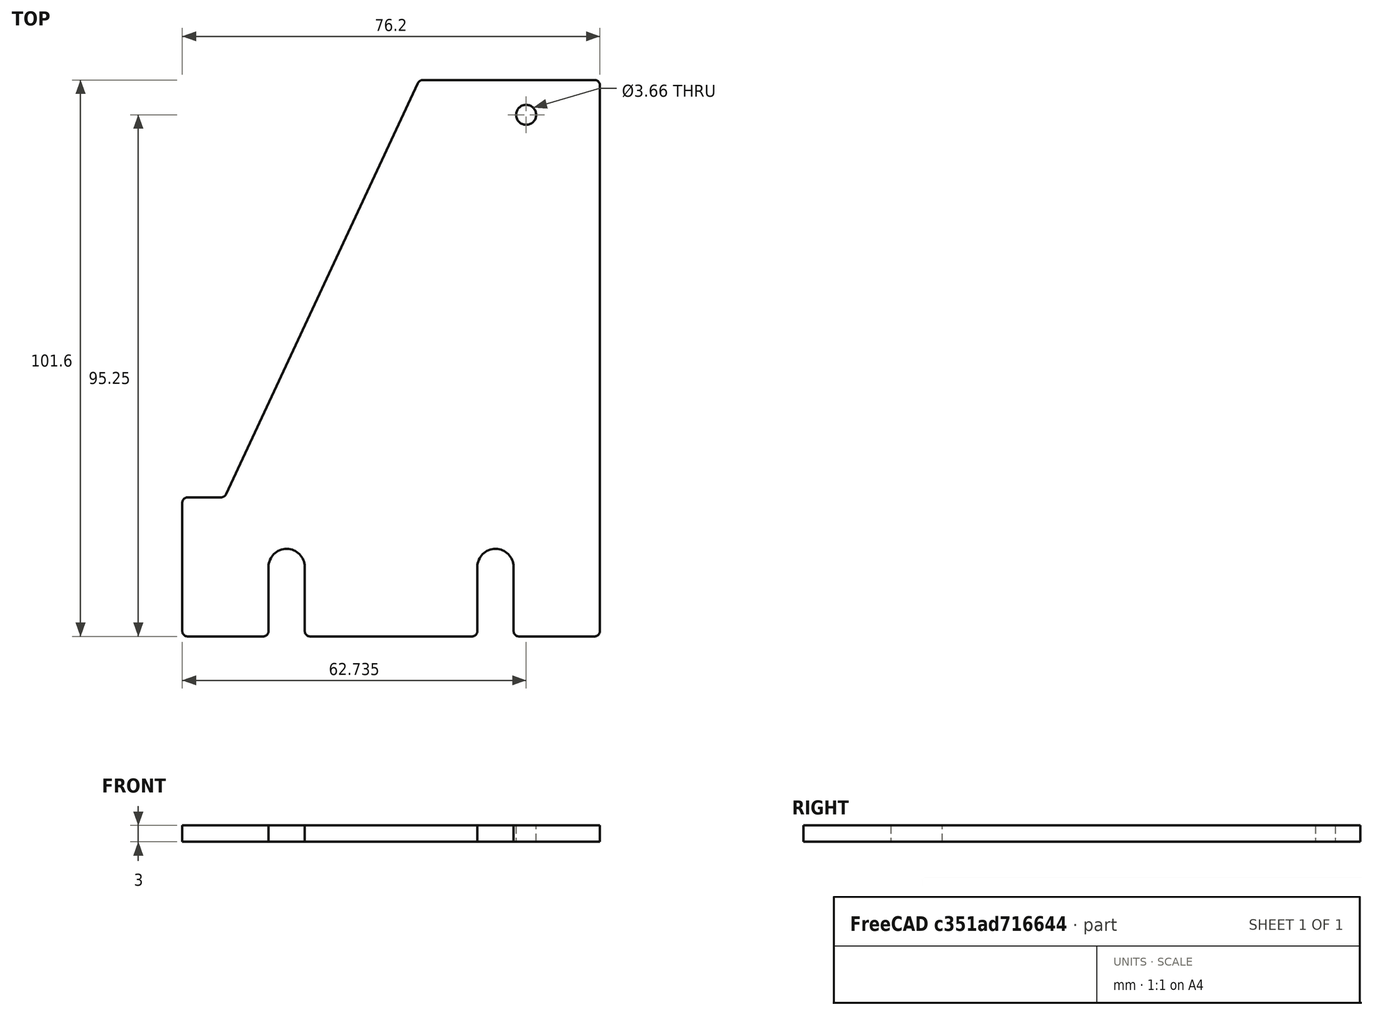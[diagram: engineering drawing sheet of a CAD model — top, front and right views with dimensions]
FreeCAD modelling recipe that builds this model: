
FCSTD DOCUMENT  (FreeCAD 0.21R33675 (Git))
Label: plain_wall_3in_with_door_angled_door_gap
License: All rights reserved
LicenseURL: http://en.wikipedia.org/wiki/All_rights_reserved
objects: Sketcher::SketchObject×1, Spreadsheet::Sheet×1, PartDesign::Pad×1, PartDesign::Body×1
note: 4 computed .brp shape members not serialized (recipe doc carries the construction recipe); baked Part::Feature solids carry a one-line shape summary decoded from their .brp

FEATURE [Sketcher::SketchObject] Sketch
  FullyConstrained = true
  MapMode = 5
  Support = -> [XY_Plane]
  expr: Constraints[15] = Spreadsheet.FilletRadius
  expr: Constraints[17] = Spreadsheet.Height
  expr: Constraints[22] = Spreadsheet.MountHoleDistanceFromBottom
  expr: Constraints[24] = Spreadsheet.MountHoleDiameter
  expr: Constraints[36] = Spreadsheet.MountHoleSideMargin
  expr: Constraints[44] = Spreadsheet.Length
  expr: Constraints[49] = Spreadsheet.DoorGap
  expr: Constraints[50] = Spreadsheet.BeamHeight
  expr: Constraints[66] = Spreadsheet.FilletRadius
  expr: Constraints[93] = Spreadsheet.BracketHoleFromSide
  expr: Constraints[97] = Spreadsheet.UpperBracketHoleFromTop
  expr: Constraints[99] = Spreadsheet.BracketHoleDiameter
  sketch-geometry (39):
    g0: ArcOfCircle CenterX=5.80048 CenterY=49.8 CenterZ=0 NormalX=0 NormalY=0 NormalZ=1 AngleXU=0 Radius=1 StartAngle=1.5708 EndAngle=2.70526
    g1: LineSegment StartX=5.80048 StartY=50.8 StartZ=0 EndX=37.1 EndY=50.8 EndZ=0
    g2: ArcOfCircle CenterX=37.1 CenterY=49.8 CenterZ=0 NormalX=0 NormalY=0 NormalZ=1 AngleXU=0 Radius=1 StartAngle=1.5e-15 EndAngle=1.5708
    g3: LineSegment StartX=38.1 StartY=49.8 StartZ=0 EndX=38.1 EndY=-49.8 EndZ=0
    g4: ArcOfCircle CenterX=37.1 CenterY=-49.8 CenterZ=0 NormalX=0 NormalY=0 NormalZ=1 AngleXU=0 Radius=1 StartAngle=4.71239 EndAngle=6.28319
    g5: LineSegment StartX=37.1 StartY=-50.8 StartZ=0 EndX=-37.1 EndY=-50.8 EndZ=0
    g6: ArcOfCircle CenterX=-37.1 CenterY=-49.8 CenterZ=0 NormalX=0 NormalY=0 NormalZ=1 AngleXU=0 Radius=1 StartAngle=3.14159 EndAngle=4.71239
    g7: GeomPoint X=-38.1 Y=50.8 Z=0
    g8: GeomPoint X=38.1 Y=-50.8 Z=0
    g9: LineSegment StartX=-19.05 StartY=-38.1 StartZ=0 EndX=19.05 EndY=-38.1 EndZ=0
    g10: LineSegment StartX=0 StartY=-50.8 StartZ=0 EndX=0 EndY=-38.1 EndZ=0
    g11: Circle CenterX=-19.05 CenterY=-38.1 CenterZ=0 NormalX=0 NormalY=0 NormalZ=1 AngleXU=0 Radius=3.302
    g12: Circle CenterX=19.05 CenterY=-38.1 CenterZ=0 NormalX=0 NormalY=0 NormalZ=1 AngleXU=0 Radius=3.302
    g13: LineSegment StartX=0 StartY=-38.1 StartZ=0 EndX=0 EndY=-50.8 EndZ=0
    g14: LineSegment StartX=-19.05 StartY=-38.1 StartZ=0 EndX=-38.1 EndY=-38.1 EndZ=0
    g15: LineSegment StartX=19.05 StartY=-38.1 StartZ=0 EndX=38.1 EndY=-38.1 EndZ=0
    g16: LineSegment StartX=-38.1 StartY=-49.8 StartZ=0 EndX=-38.1 EndY=-26.4 EndZ=0
    g17: ArcOfCircle CenterX=-37.1 CenterY=-26.4 CenterZ=0 NormalX=0 NormalY=0 NormalZ=1 AngleXU=0 Radius=1 StartAngle=1.5708 EndAngle=3.14159
    g18: LineSegment StartX=-37.1 StartY=-25.4 StartZ=0 EndX=-31.0063 EndY=-25.4 EndZ=0
    g19: LineSegment StartX=4.89417 StartY=50.2226 StartZ=0 EndX=-30.1 EndY=-24.8226 EndZ=0
    g20: ArcOfCircle CenterX=-31.0063 CenterY=-24.4 CenterZ=0 NormalX=0 NormalY=0 NormalZ=1 AngleXU=0 Radius=1 StartAngle=4.71239 EndAngle=5.84685
    g21: ArcOfCircle CenterX=-19.05 CenterY=-38.1 CenterZ=0 NormalX=0 NormalY=0 NormalZ=1 AngleXU=0 Radius=3.302 StartAngle=0 EndAngle=3.14159
    g22: LineSegment StartX=-22.352 StartY=-38.1 StartZ=0 EndX=-22.352 EndY=-49.8 EndZ=0
    g23: LineSegment StartX=-15.748 StartY=-38.1 StartZ=0 EndX=-15.748 EndY=-49.8 EndZ=0
    g24: ArcOfCircle CenterX=-23.352 CenterY=-49.8 CenterZ=0 NormalX=0 NormalY=0 NormalZ=1 AngleXU=0 Radius=1 StartAngle=4.71239 EndAngle=6.28319
    g25: ArcOfCircle CenterX=-14.748 CenterY=-49.8 CenterZ=0 NormalX=0 NormalY=0 NormalZ=1 AngleXU=0 Radius=1 StartAngle=3.14159 EndAngle=4.71239
    g26: ArcOfCircle CenterX=19.05 CenterY=-38.1 CenterZ=0 NormalX=0 NormalY=0 NormalZ=1 AngleXU=0 Radius=3.302 StartAngle=-9e-16 EndAngle=3.14159
    g27: LineSegment StartX=15.748 StartY=-38.1 StartZ=0 EndX=15.748 EndY=-49.8 EndZ=0
    g28: LineSegment StartX=22.352 StartY=-38.1 StartZ=0 EndX=22.352 EndY=-49.8 EndZ=0
    g29: ArcOfCircle CenterX=14.748 CenterY=-49.8 CenterZ=0 NormalX=0 NormalY=0 NormalZ=1 AngleXU=0 Radius=1 StartAngle=4.71239 EndAngle=6.28319
    g30: ArcOfCircle CenterX=23.352 CenterY=-49.8 CenterZ=0 NormalX=0 NormalY=0 NormalZ=1 AngleXU=0 Radius=1 StartAngle=3.14159 EndAngle=4.71239
    g31: LineSegment StartX=-37.1 StartY=-50.8 StartZ=0 EndX=-23.352 EndY=-50.8 EndZ=0
    g32: LineSegment StartX=-14.748 StartY=-50.8 StartZ=0 EndX=14.748 EndY=-50.8 EndZ=0
    g33: LineSegment StartX=23.352 StartY=-50.8 StartZ=0 EndX=37.1 EndY=-50.8 EndZ=0
    g34: LineSegment StartX=37.1 StartY=50.8 StartZ=0 EndX=38.1 EndY=50.8 EndZ=0
    g35: LineSegment StartX=38.1 StartY=49.8 StartZ=0 EndX=38.1 EndY=50.8 EndZ=0
    g36: LineSegment StartX=38.1 StartY=50.8 StartZ=0 EndX=24.6352 EndY=50.8 EndZ=0
    g37: LineSegment StartX=24.6352 StartY=50.8 StartZ=0 EndX=24.6352 EndY=44.45 EndZ=0
    g38: Circle CenterX=24.6352 CenterY=44.45 CenterZ=0 NormalX=0 NormalY=0 NormalZ=1 AngleXU=0 Radius=1.8288
  constraints (100):
    c: Tangent(g0,g1) = 1.5708
    c: Tangent(g1,g2) = 1.5708
    c: Tangent(g2,g3) = 1.5708
    c: Tangent(g3,g4) = 1.5708
    c: Tangent(g4,g5) = 1.5708
    c: Tangent(g5,g6) = 1.5708
    c: Horizontal(g1)
    c: Horizontal(g5)
    c: Vertical(g3)
    c: Equal(g0,g2)
    c: Equal(g2,g4)
    c: Equal(g4,g6)
    c: PointOnObject(g7,g1)
    c: PointOnObject(g8,g3)
    c: PointOnObject(g8,g5)
    c: Radius(g2) = 1
    c: Symmetric(g7,g8,g-1)
    c: DistanceY(g4,g1) = 101.6
    c: Horizontal(g9)
    c: Vertical(g10)
    c: PointOnObject(g10,g5)
    c: PointOnObject(g10,g-2)
    c: DistanceY(g10,g10) = 12.7
    c: Coincident(g12,g9)
    c: Diameter(g12) = 6.604
    c: Equal(g11,g12)
    c: Coincident(g11,g9)
    c: PointOnObject(g13,g9)
    c: Vertical(g13)
    c: Coincident(g13,g10)
    c: Coincident(g14,g11)
    c: Horizontal(g14)
    c: Coincident(g15,g12)
    c: PointOnObject(g15,g3)
    c: Horizontal(g15)
    c: Equal(g15,g14)
    c: DistanceX(g14,g14) = 19.05
    c: Vertical(g16)
    c: PointOnObject(g14,g16)
    c: Tangent(g17,g16) = 1.5708
    c: Horizontal(g18)
    c: Tangent(g18,g17) = 1.5708
    c: Equal(g17,g6)
    c: Tangent(g0,g19) = -1.5708
    c: DistanceX(g6,g3) = 76.2
    c: Symmetric(g11,g12,g10)
    c: Tangent(g20,g18) = -1.5708
    c: Tangent(g20,g19) = 1.5708
    c: Equal(g20,g17)
    c: DistanceX(g16,g19) = 8
    c: DistanceY(g5,g17) = 25.4
    c: Tangent(g16,g6) = 1.5708
    c: Angle(g19,g18) = 2.00713
    c: Coincident(g21,g9)
    c: PointOnObject(g21,g14)
    c: PointOnObject(g21,g9)
    c: PointOnObject(g21,g11)
    c: Vertical(g22)
    c: Vertical(g23)
    c: Coincident(g22,g21)
    c: Coincident(g23,g21)
    c: Equal(g22,g23)
    c: Tangent(g24,g22) = 1.5708
    c: Tangent(g24,g5) = 1.5708
    c: Tangent(g25,g23) = -1.5708
    c: Tangent(g25,g5) = 1.5708
    c: Radius(g24) = 1
    c: Coincident(g26,g9)
    c: PointOnObject(g26,g9)
    c: PointOnObject(g26,g15)
    c: PointOnObject(g26,g12)
    c: Vertical(g27)
    c: Vertical(g28)
    c: Coincident(g27,g26)
    c: Coincident(g26,g28)
    c: Equal(g27,g28)
    c: Tangent(g29,g27) = 1.5708
    c: Tangent(g29,g5) = 1.5708
    c: Tangent(g30,g28) = -1.5708
    c: Tangent(g30,g5) = 1.5708
    c: Equal(g29,g25)
    c: Coincident(g31,g6)
    c: Coincident(g31,g24)
    c: Coincident(g32,g25)
    c: Coincident(g29,g32)
    c: Coincident(g33,g30)
    c: Coincident(g33,g4)
    c: Coincident(g34,g1)
    c: Horizontal(g34)
    c: Coincident(g35,g2)
    c: Vertical(g35)
    c: Coincident(g35,g34)
    c: Coincident(g36,g34)
    c: DistanceX(g36,g36) = 13.4648
    c: Horizontal(g36)
    c: Coincident(g37,g36)
    c: Vertical(g37)
    c: DistanceY(g37,g37) = 6.35
    c: Coincident(g37,g38)
    c: Diameter(g38) = 3.6576
FEATURE [Spreadsheet::Sheet] Spreadsheet
  cells = A2='Parameters; A3='Height; B3(Height)==4 in; A4='Length; B4(Length)==3 in; A5='Thickness; B5(Thickness)==3 mm; A6='FilletRadius; B6(FilletRadius)==1 mm; A7='MountHoleDiameter; B7(MountHoleDiameter)==0.26 in; A8='MountHoleDistanceFromBottom; B8(MountHoleDistanceFromBottom)==0.5 in; A9='MountHoleSideMargin; B9(MountHoleSideMargin)==0.75 in; A10='BeamHeight; B10(BeamHeight)==1 in; A11='DoorGap; B11(DoorGap)==8 mm; A13='BracketWidth; B13(BracketWidth)==0.5 in; A14='BracketHoleDiameter; B14(BracketHoleDiameter)==0.144 in; A15='BracketHoleOffset; B15(BracketHoleOffset)==0.412 in; A16='UpperBracketHoleFromTop; B16(UpperBracketHoleFromTop)==0.5 * BracketWidth; A17='BracketHoleFromSide; B17(BracketHoleFromSide)==BracketHoleOffset + Thickness
FEATURE [PartDesign::Pad] Pad
  Direction = (0,0,1)
  Length = 3
  Length2 = 10
  Profile = -> Sketch
  ReferenceAxis = -> Sketch [N_Axis]
  Type = 0
  expr: Length = Spreadsheet.Thickness
FEATURE [PartDesign::Body] Body
  Group = -> [Sketch,Pad]
  Origin = -> Origin
  Tip = -> Pad
